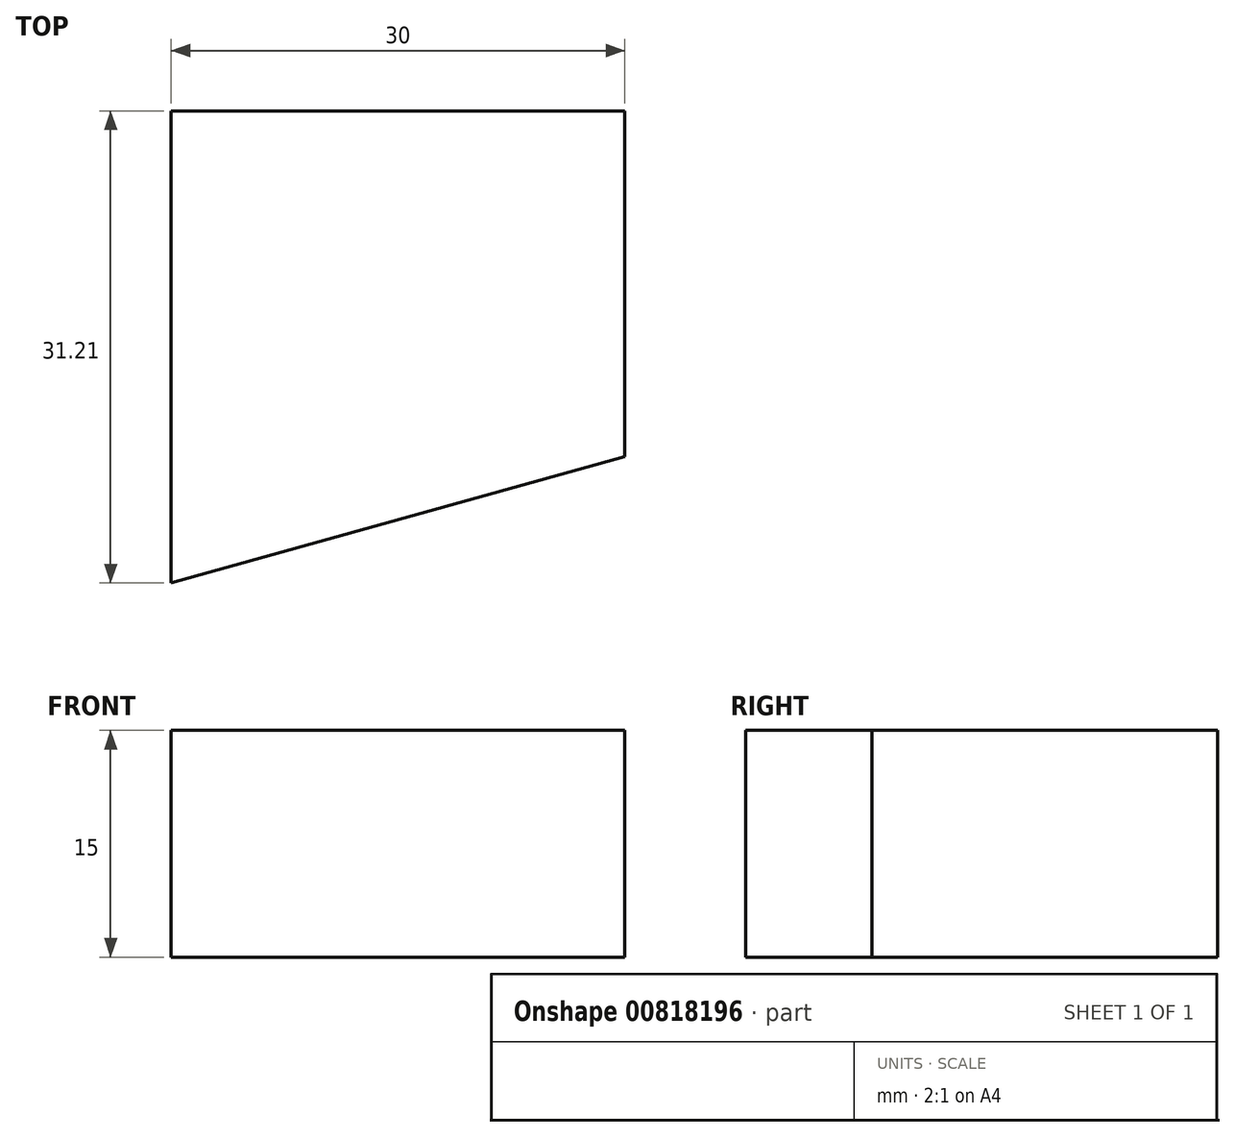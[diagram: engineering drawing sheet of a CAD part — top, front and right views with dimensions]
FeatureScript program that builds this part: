
annotation { "Feature Type Name" : "Feature", "Feature Type Description" : "" }
export const myFeature = defineFeature(function(context is Context, id is Id, definition is map)
    precondition{}
    {
        {
            var Q0;
            Q0=qCreatedBy(makeId("Top.planeOp"),FACE);
            var sketch = newSketch(context, id + "F0", { "sketchPlane" : qUnion([Q0])});
            skLineSegment(sketch, "E0.bottom", {"start": v(0, 0) * mm, "end": v(70, 0) * mm});
            skLineSegment(sketch, "E0.top", {"start": v(0, -90) * mm, "end": v(70, -90) * mm});
            skLineSegment(sketch, "E0.left", {"start": v(0, 0) * mm, "end": v(0, -90) * mm});
            skLineSegment(sketch, "E0.right", {"start": v(70, 0) * mm, "end": v(70, -90) * mm});
            skSolve(sketch);
        }
        {
            var Q0;
            Q0=makeQuery(id+"F0.imprint","IMPRINT",FACE,{"disambiguationData":[TD([[makeQuery(id+"F0.imprint","IMPRINT",EDGE,{"derivedFrom":sQuery(id+"F0.wireOp",EDGE,"E0.bottom")}),-1.0]])]});
            extrude(context, id + "F1", {"entities" : qUnion([Q0]), "depth" : 15 * mm, "offsetDistance" : 25 * mm});
        }
        {
            var Q0;
            Q0=makeQuery(id+"F1.opExtrude","CAP_FACE",FACE,{"disambiguationData":[OSD([sQuery(id+"F0.wireOp",EDGE,"E0.bottom"),sQuery(id+"F0.wireOp",EDGE,"E0.top"),sQuery(id+"F0.wireOp",EDGE,"E0.left"),sQuery(id+"F0.wireOp",EDGE,"E0.right")])],"isStart":false});
            var sketch = newSketch(context, id + "F2", { "sketchPlane" : qUnion([Q0])});
            skLineSegment(sketch, "E1", {"start": v(0, 0) * mm, "end": v(0, -10) * mm});
            skLineSegment(sketch, "E2", {"start": v(0, -10) * mm, "end": v(30, -10) * mm});
            skLineSegment(sketch, "E3", {"start": v(30, -10) * mm, "end": v(30, 0) * mm});
            skLineSegment(sketch, "E4", {"start": v(30, 0) * mm, "end": v(0, 0) * mm});
            skLineSegment(sketch, "E5.bottom", {"start": v(30, 0) * mm, "end": v(40, 0) * mm});
            skLineSegment(sketch, "E5.top", {"start": v(30, -10) * mm, "end": v(40, -10) * mm});
            skLineSegment(sketch, "E5.left", {"start": v(30, 0) * mm, "end": v(30, -10) * mm});
            skLineSegment(sketch, "E5.right", {"start": v(40, 0) * mm, "end": v(40, -10) * mm});
            skLineSegment(sketch, "E6.bottom", {"start": v(40, 0) * mm, "end": v(50, 0) * mm});
            skLineSegment(sketch, "E6.top", {"start": v(40, -10) * mm, "end": v(50, -10) * mm});
            skLineSegment(sketch, "E6.right", {"start": v(50, 0) * mm, "end": v(50, -10) * mm});
            skLineSegment(sketch, "E7.bottom", {"start": v(0, -10) * mm, "end": v(10, -10) * mm});
            skLineSegment(sketch, "E7.top", {"start": v(0, -20) * mm, "end": v(10, -20) * mm});
            skLineSegment(sketch, "E7.left", {"start": v(0, -10) * mm, "end": v(0, -20) * mm});
            skLineSegment(sketch, "E7.right", {"start": v(10, -10) * mm, "end": v(10, -20) * mm});
            skLineSegment(sketch, "E8", {"start": v(0, -90) * mm, "end": v(0, -63) * mm});
            skLineSegment(sketch, "E9", {"start": v(0, -63) * mm, "end": v(70, -82.5) * mm});
            skLineSegment(sketch, "E10", {"start": v(0, -63) * mm, "end": v(0, -44) * mm});
            skLineSegment(sketch, "E11", {"start": v(0, -44) * mm, "end": v(70, -24.5) * mm});
            skLineSegment(sketch, "E12", {"start": v(70, -24.5) * mm, "end": v(70, -82.5) * mm});
            skLineSegment(sketch, "E13", {"start": v(50, -10) * mm, "end": v(50, -30.07) * mm});
            skLineSegment(sketch, "E14", {"start": v(40, -10) * mm, "end": v(40, -32.86) * mm});
            skLineSegment(sketch, "E15", {"start": v(0, 0) * mm, "end": v(20, 0) * mm});
            skLineSegment(sketch, "E16", {"start": v(10, -20) * mm, "end": v(10, -41.21) * mm});
            skSolve(sketch);
        }
        {
            var Q0;
            Q0=makeQuery(id+"F2.imprint","IMPRINT",FACE,{"disambiguationData":[TD([[makeQuery(id+"F2.imprint","IMPRINT",EDGE,{"derivedFrom":sQuery(id+"F2.wireOp",EDGE,"E1")}),1.0]])]});
            var Q1;
            Q1=makeQuery(id+"F2.imprint","IMPRINT",FACE,{"disambiguationData":[TD([[makeQuery(id+"F2.imprint","IMPRINT",EDGE,{"derivedFrom":sQuery(id+"F2.wireOp",EDGE,"E5.bottom")}),-1.0]])]});
            var Q2;
            Q2=makeQuery(id+"F2.imprint","IMPRINT",FACE,{"disambiguationData":[TD([[makeQuery(id+"F2.imprint","IMPRINT",EDGE,{"derivedFrom":sQuery(id+"F2.wireOp",EDGE,"E6.bottom")}),-1.0]])]});
            var Q3;
            {var subQ3=sQuery(id+"F2.wireOp",EDGE,"E6.right");Q3=makeQuery(id+"F2.imprint","IMPRINT",FACE,{"disambiguationData":[TD([[makeQuery(id+"F2.imprint","IMPRINT",EDGE,{"derivedFrom":subQ3}),1.0]])]});}
            var Q4;
            Q4=makeQuery(id+"F2.imprint","IMPRINT",FACE,{"disambiguationData":[TD([[makeQuery(id+"F2.imprint","IMPRINT",EDGE,{"derivedFrom":sQuery(id+"F2.wireOp",EDGE,"E6.top")}),-1.0]])]});
            var Q5;
            Q5=makeQuery(id+"F2.imprint","IMPRINT",FACE,{"disambiguationData":[TD([[makeQuery(id+"F2.imprint","IMPRINT",EDGE,{"derivedFrom":sQuery(id+"F2.wireOp",EDGE,"E2")}),-1.0]])]});
            var Q6;
            {var subQ0=sQuery(id+"F2.wireOp",EDGE,"E7.top");Q6=makeQuery(id+"F2.imprint","IMPRINT",FACE,{"disambiguationData":[TD([[makeQuery(id+"F2.imprint","IMPRINT",EDGE,{"derivedFrom":subQ0}),-1.0]])]});}
            var Q7;
            Q7=makeQuery(id+"F2.imprint","IMPRINT",FACE,{"disambiguationData":[TD([[makeQuery(id+"F2.imprint","IMPRINT",EDGE,{"derivedFrom":sQuery(id+"F2.wireOp",EDGE,"E9")}),1.0]])]});
            var Q8;
            Q8=makeQuery(id+"F2.imprint","IMPRINT",FACE,{"disambiguationData":[TD([[makeQuery(id+"F2.imprint","IMPRINT",EDGE,{"derivedFrom":sQuery(id+"F2.wireOp",EDGE,"E8")}),1.0]])]});
            extrude(context, id + "F3", {"entities" : qUnion([Q0, Q1, Q2, Q3, Q4, Q5, Q6, Q7, Q8]), "operationType" : NewBodyOperationType.REMOVE, "oppositeDirection" : true, "depth" : 25 * mm, "offsetDistance" : 25 * mm});
        }
    });
